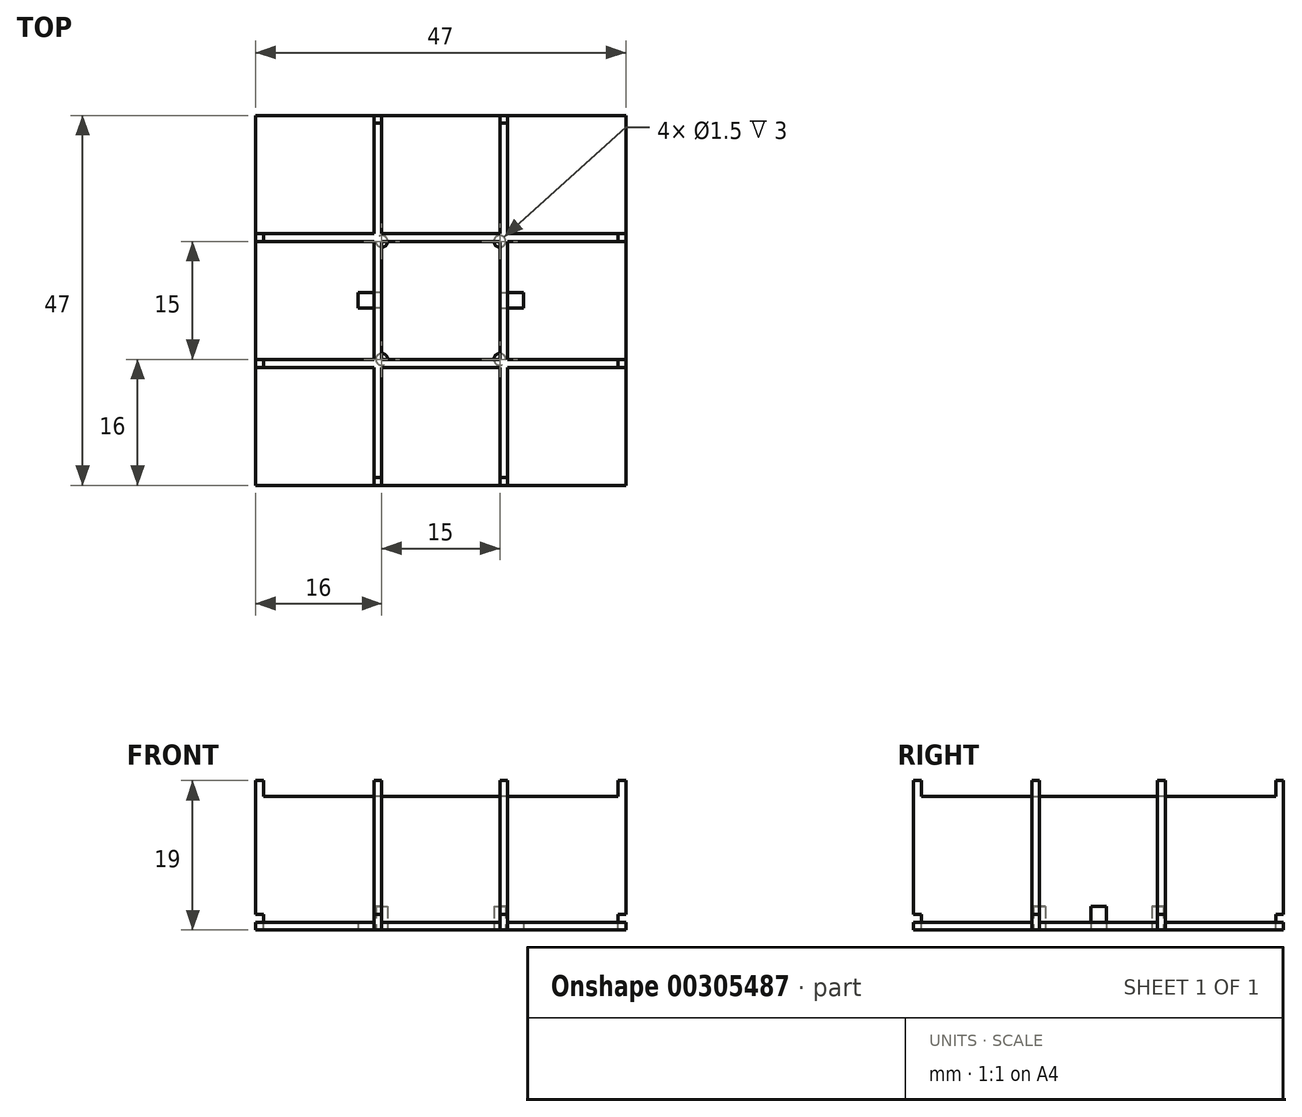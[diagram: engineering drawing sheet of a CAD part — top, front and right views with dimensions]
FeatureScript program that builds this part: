
annotation { "Feature Type Name" : "Feature", "Feature Type Description" : "" }
export const myFeature = defineFeature(function(context is Context, id is Id, definition is map)
    precondition{}
    {
        {
            var Q0;
            Q0=qCreatedBy(makeId("Top.planeOp"),FACE);
            var sketch = newSketch(context, id + "F0", { "sketchPlane" : qUnion([Q0])});
            skLineSegment(sketch, "E0.bottom", {"start": v(-23.5, 23.5) * mm, "end": v(23.5, 23.5) * mm});
            skLineSegment(sketch, "E0.top", {"start": v(-23.5, -23.5) * mm, "end": v(23.5, -23.5) * mm});
            skLineSegment(sketch, "E0.left", {"start": v(-23.5, 23.5) * mm, "end": v(-23.5, -23.5) * mm});
            skLineSegment(sketch, "E0.right", {"start": v(23.5, 23.5) * mm, "end": v(23.5, -23.5) * mm});
            skLineSegment(sketch, "E1", {"start": v(0, 26.11) * mm, "end": v(0, -40.09) * mm, "construction": true});
            skLineSegment(sketch, "E2", {"start": v(37.07, 0) * mm, "end": v(-38.69, 0) * mm, "construction": true});
            skLineSegment(sketch, "E3", {"start": v(-23.5, 8.5) * mm, "end": v(23.5, 8.5) * mm});
            skLineSegment(sketch, "E4", {"start": v(23.5, -8.5) * mm, "end": v(-23.5, -8.5) * mm});
            skLineSegment(sketch, "E5", {"start": v(-8.5, 23.5) * mm, "end": v(-8.5, -23.5) * mm});
            skLineSegment(sketch, "E6", {"start": v(8.5, 23.5) * mm, "end": v(8.5, -23.5) * mm});
            skLineSegment(sketch, "E7.0", {"start": v(-23.5, 7.5) * mm, "end": v(23.5, 7.5) * mm});
            skLineSegment(sketch, "E8.0", {"start": v(23.5, -7.5) * mm, "end": v(-23.5, -7.5) * mm});
            skLineSegment(sketch, "E9.0", {"start": v(-7.5, 23.5) * mm, "end": v(-7.5, -23.5) * mm});
            skLineSegment(sketch, "E10.0", {"start": v(7.5, 23.5) * mm, "end": v(7.5, -23.5) * mm});
            skSolve(sketch);
        }
        {
            var Q0;
            {var subQ0=sQuery(id+"F0.wireOp",EDGE,"E7.0");var subQ1=sQuery(id+"F0.wireOp",EDGE,"E6");var subQ2=makeQuery(id+"F0.imprint","INTERSECT",VERTEX,{"derivedFrom":[subQ1,subQ0]});Q0=makeQuery(id+"F0.imprint","IMPRINT",FACE,{"disambiguationData":[TD([[makeQuery(id+"F0.imprint","IMPRINT",EDGE,{"disambiguationData":[TD([[subQ2,-1.0]])],"derivedFrom":subQ1}),-1.0]])]});}
            var Q1;
            {var subQ0=sQuery(id+"F0.wireOp",EDGE,"E4");var subQ1=sQuery(id+"F0.wireOp",EDGE,"E0.left");var subQ2=makeQuery(id+"F0.imprint","INTERSECT",VERTEX,{"derivedFrom":[subQ1,subQ0]});Q1=makeQuery(id+"F0.imprint","IMPRINT",FACE,{"disambiguationData":[TD([[makeQuery(id+"F0.imprint","IMPRINT",EDGE,{"disambiguationData":[TD([[subQ2,1.0]])],"derivedFrom":subQ1}),1.0]])]});}
            var Q2;
            {var subQ0=sQuery(id+"F0.wireOp",EDGE,"E7.0");var subQ1=sQuery(id+"F0.wireOp",EDGE,"E0.left");var subQ2=makeQuery(id+"F0.imprint","INTERSECT",VERTEX,{"derivedFrom":[subQ1,subQ0]});Q2=makeQuery(id+"F0.imprint","IMPRINT",FACE,{"disambiguationData":[TD([[makeQuery(id+"F0.imprint","IMPRINT",EDGE,{"disambiguationData":[TD([[subQ2,-1.0]])],"derivedFrom":subQ1}),1.0]])]});}
            var Q3;
            {var subQ0=sQuery(id+"F0.wireOp",EDGE,"E6");var subQ1=sQuery(id+"F0.wireOp",EDGE,"E0.top");var subQ2=makeQuery(id+"F0.imprint","INTERSECT",VERTEX,{"derivedFrom":[subQ1,subQ0]});Q3=makeQuery(id+"F0.imprint","IMPRINT",FACE,{"disambiguationData":[TD([[makeQuery(id+"F0.imprint","IMPRINT",EDGE,{"disambiguationData":[TD([[subQ2,1.0]])],"derivedFrom":subQ1}),1.0]])]});}
            var Q4;
            {var subQ0=sQuery(id+"F0.wireOp",EDGE,"E9.0");var subQ1=sQuery(id+"F0.wireOp",EDGE,"E0.top");var subQ2=makeQuery(id+"F0.imprint","INTERSECT",VERTEX,{"derivedFrom":[subQ1,subQ0]});Q4=makeQuery(id+"F0.imprint","IMPRINT",FACE,{"disambiguationData":[TD([[makeQuery(id+"F0.imprint","IMPRINT",EDGE,{"disambiguationData":[TD([[subQ2,-1.0]])],"derivedFrom":subQ1}),1.0]])]});}
            var Q5;
            {var subQ0=sQuery(id+"F0.wireOp",EDGE,"E5");var subQ1=sQuery(id+"F0.wireOp",EDGE,"E0.top");var subQ2=makeQuery(id+"F0.imprint","INTERSECT",VERTEX,{"derivedFrom":[subQ1,subQ0]});Q5=makeQuery(id+"F0.imprint","IMPRINT",FACE,{"disambiguationData":[TD([[makeQuery(id+"F0.imprint","IMPRINT",EDGE,{"disambiguationData":[TD([[subQ2,-1.0]])],"derivedFrom":subQ1}),1.0]])]});}
            var Q6;
            {var subQ0=sQuery(id+"F0.wireOp",EDGE,"E0.right");var subQ1=sQuery(id+"F0.wireOp",EDGE,"E0.top");var subQ2=makeQuery(id+"F0.imprint","INTERSECT",VERTEX,{"derivedFrom":[subQ1,subQ0]});Q6=makeQuery(id+"F0.imprint","IMPRINT",FACE,{"disambiguationData":[TD([[makeQuery(id+"F0.imprint","IMPRINT",EDGE,{"disambiguationData":[TD([[subQ2,1.0]])],"derivedFrom":subQ1}),1.0]])]});}
            var Q7;
            {var subQ0=sQuery(id+"F0.wireOp",EDGE,"E0.left");var subQ1=sQuery(id+"F0.wireOp",EDGE,"E0.top");var subQ2=makeQuery(id+"F0.imprint","INTERSECT",VERTEX,{"derivedFrom":[subQ1,subQ0]});Q7=makeQuery(id+"F0.imprint","IMPRINT",FACE,{"disambiguationData":[TD([[makeQuery(id+"F0.imprint","IMPRINT",EDGE,{"disambiguationData":[TD([[subQ2,-1.0]])],"derivedFrom":subQ1}),1.0]])]});}
            var Q8;
            {var subQ0=sQuery(id+"F0.wireOp",EDGE,"E7.0");var subQ1=sQuery(id+"F0.wireOp",EDGE,"E0.right");var subQ2=makeQuery(id+"F0.imprint","INTERSECT",VERTEX,{"derivedFrom":[subQ1,subQ0]});Q8=makeQuery(id+"F0.imprint","IMPRINT",FACE,{"disambiguationData":[TD([[makeQuery(id+"F0.imprint","IMPRINT",EDGE,{"disambiguationData":[TD([[subQ2,-1.0]])],"derivedFrom":subQ1}),-1.0]])]});}
            var Q9;
            {var subQ0=sQuery(id+"F0.wireOp",EDGE,"E4");var subQ1=sQuery(id+"F0.wireOp",EDGE,"E0.right");var subQ2=makeQuery(id+"F0.imprint","INTERSECT",VERTEX,{"derivedFrom":[subQ1,subQ0]});Q9=makeQuery(id+"F0.imprint","IMPRINT",FACE,{"disambiguationData":[TD([[makeQuery(id+"F0.imprint","IMPRINT",EDGE,{"disambiguationData":[TD([[subQ2,1.0]])],"derivedFrom":subQ1}),-1.0]])]});}
            var Q10;
            {var subQ0=sQuery(id+"F0.wireOp",EDGE,"E10.0");var subQ1=sQuery(id+"F0.wireOp",EDGE,"E4");var subQ2=makeQuery(id+"F0.imprint","INTERSECT",VERTEX,{"derivedFrom":[subQ1,subQ0]});Q10=makeQuery(id+"F0.imprint","IMPRINT",FACE,{"disambiguationData":[TD([[makeQuery(id+"F0.imprint","IMPRINT",EDGE,{"disambiguationData":[TD([[subQ2,-1.0]])],"derivedFrom":subQ1}),-1.0]])]});}
            var Q11;
            {var subQ0=sQuery(id+"F0.wireOp",EDGE,"E7.0");var subQ1=sQuery(id+"F0.wireOp",EDGE,"E5");var subQ2=makeQuery(id+"F0.imprint","INTERSECT",VERTEX,{"derivedFrom":[subQ1,subQ0]});Q11=makeQuery(id+"F0.imprint","IMPRINT",FACE,{"disambiguationData":[TD([[makeQuery(id+"F0.imprint","IMPRINT",EDGE,{"disambiguationData":[TD([[subQ2,-1.0]])],"derivedFrom":subQ1}),1.0]])]});}
            var Q12;
            {var subQ0=sQuery(id+"F0.wireOp",EDGE,"E9.0");var subQ1=sQuery(id+"F0.wireOp",EDGE,"E7.0");var subQ2=makeQuery(id+"F0.imprint","INTERSECT",VERTEX,{"derivedFrom":[subQ1,subQ0]});Q12=makeQuery(id+"F0.imprint","IMPRINT",FACE,{"disambiguationData":[TD([[makeQuery(id+"F0.imprint","IMPRINT",EDGE,{"disambiguationData":[TD([[subQ2,-1.0]])],"derivedFrom":subQ1}),-1.0]])]});}
            var Q13;
            {var subQ0=sQuery(id+"F0.wireOp",EDGE,"E6");var subQ1=sQuery(id+"F0.wireOp",EDGE,"E4");var subQ2=makeQuery(id+"F0.imprint","INTERSECT",VERTEX,{"derivedFrom":[subQ1,subQ0]});Q13=makeQuery(id+"F0.imprint","IMPRINT",FACE,{"disambiguationData":[TD([[makeQuery(id+"F0.imprint","IMPRINT",EDGE,{"disambiguationData":[TD([[subQ2,-1.0]])],"derivedFrom":subQ1}),-1.0]])]});}
            var Q14;
            {var subQ0=sQuery(id+"F0.wireOp",EDGE,"E9.0");var subQ1=sQuery(id+"F0.wireOp",EDGE,"E4");var subQ2=makeQuery(id+"F0.imprint","INTERSECT",VERTEX,{"derivedFrom":[subQ1,subQ0]});Q14=makeQuery(id+"F0.imprint","IMPRINT",FACE,{"disambiguationData":[TD([[makeQuery(id+"F0.imprint","IMPRINT",EDGE,{"disambiguationData":[TD([[subQ2,-1.0]])],"derivedFrom":subQ1}),-1.0]])]});}
            var Q15;
            {var subQ0=sQuery(id+"F0.wireOp",EDGE,"E5");var subQ1=sQuery(id+"F0.wireOp",EDGE,"E3");var subQ2=makeQuery(id+"F0.imprint","INTERSECT",VERTEX,{"derivedFrom":[subQ1,subQ0]});Q15=makeQuery(id+"F0.imprint","IMPRINT",FACE,{"disambiguationData":[TD([[makeQuery(id+"F0.imprint","IMPRINT",EDGE,{"disambiguationData":[TD([[subQ2,-1.0]])],"derivedFrom":subQ1}),-1.0]])]});}
            var Q16;
            {var subQ0=sQuery(id+"F0.wireOp",EDGE,"E3");var subQ1=sQuery(id+"F0.wireOp",EDGE,"E0.left");var subQ2=makeQuery(id+"F0.imprint","INTERSECT",VERTEX,{"derivedFrom":[subQ1,subQ0]});Q16=makeQuery(id+"F0.imprint","IMPRINT",FACE,{"disambiguationData":[TD([[makeQuery(id+"F0.imprint","IMPRINT",EDGE,{"disambiguationData":[TD([[subQ2,-1.0]])],"derivedFrom":subQ1}),1.0]])]});}
            var Q17;
            {var subQ0=sQuery(id+"F0.wireOp",EDGE,"E6");var subQ1=sQuery(id+"F0.wireOp",EDGE,"E0.bottom");var subQ2=makeQuery(id+"F0.imprint","INTERSECT",VERTEX,{"derivedFrom":[subQ1,subQ0]});Q17=makeQuery(id+"F0.imprint","IMPRINT",FACE,{"disambiguationData":[TD([[makeQuery(id+"F0.imprint","IMPRINT",EDGE,{"disambiguationData":[TD([[subQ2,1.0]])],"derivedFrom":subQ1}),-1.0]])]});}
            var Q18;
            {var subQ0=sQuery(id+"F0.wireOp",EDGE,"E9.0");var subQ1=sQuery(id+"F0.wireOp",EDGE,"E0.bottom");var subQ2=makeQuery(id+"F0.imprint","INTERSECT",VERTEX,{"derivedFrom":[subQ1,subQ0]});Q18=makeQuery(id+"F0.imprint","IMPRINT",FACE,{"disambiguationData":[TD([[makeQuery(id+"F0.imprint","IMPRINT",EDGE,{"disambiguationData":[TD([[subQ2,-1.0]])],"derivedFrom":subQ1}),-1.0]])]});}
            var Q19;
            {var subQ0=sQuery(id+"F0.wireOp",EDGE,"E5");var subQ1=sQuery(id+"F0.wireOp",EDGE,"E0.bottom");var subQ2=makeQuery(id+"F0.imprint","INTERSECT",VERTEX,{"derivedFrom":[subQ1,subQ0]});Q19=makeQuery(id+"F0.imprint","IMPRINT",FACE,{"disambiguationData":[TD([[makeQuery(id+"F0.imprint","IMPRINT",EDGE,{"disambiguationData":[TD([[subQ2,-1.0]])],"derivedFrom":subQ1}),-1.0]])]});}
            var Q20;
            {var subQ0=sQuery(id+"F0.wireOp",EDGE,"E0.right");var subQ1=sQuery(id+"F0.wireOp",EDGE,"E0.bottom");var subQ2=makeQuery(id+"F0.imprint","INTERSECT",VERTEX,{"derivedFrom":[subQ1,subQ0]});Q20=makeQuery(id+"F0.imprint","IMPRINT",FACE,{"disambiguationData":[TD([[makeQuery(id+"F0.imprint","IMPRINT",EDGE,{"disambiguationData":[TD([[subQ2,1.0]])],"derivedFrom":subQ1}),-1.0]])]});}
            var Q21;
            {var subQ0=sQuery(id+"F0.wireOp",EDGE,"E3");var subQ1=sQuery(id+"F0.wireOp",EDGE,"E0.right");var subQ2=makeQuery(id+"F0.imprint","INTERSECT",VERTEX,{"derivedFrom":[subQ1,subQ0]});Q21=makeQuery(id+"F0.imprint","IMPRINT",FACE,{"disambiguationData":[TD([[makeQuery(id+"F0.imprint","IMPRINT",EDGE,{"disambiguationData":[TD([[subQ2,-1.0]])],"derivedFrom":subQ1}),-1.0]])]});}
            var Q22;
            {var subQ0=sQuery(id+"F0.wireOp",EDGE,"E0.left");var subQ1=sQuery(id+"F0.wireOp",EDGE,"E0.bottom");var subQ2=makeQuery(id+"F0.imprint","INTERSECT",VERTEX,{"derivedFrom":[subQ1,subQ0]});Q22=makeQuery(id+"F0.imprint","IMPRINT",FACE,{"disambiguationData":[TD([[makeQuery(id+"F0.imprint","IMPRINT",EDGE,{"disambiguationData":[TD([[subQ2,-1.0]])],"derivedFrom":subQ1}),-1.0]])]});}
            var Q23;
            {var subQ0=sQuery(id+"F0.wireOp",EDGE,"E10.0");var subQ1=sQuery(id+"F0.wireOp",EDGE,"E3");var subQ2=makeQuery(id+"F0.imprint","INTERSECT",VERTEX,{"derivedFrom":[subQ1,subQ0]});Q23=makeQuery(id+"F0.imprint","IMPRINT",FACE,{"disambiguationData":[TD([[makeQuery(id+"F0.imprint","IMPRINT",EDGE,{"disambiguationData":[TD([[subQ2,-1.0]])],"derivedFrom":subQ1}),-1.0]])]});}
            var Q24;
            {var subQ0=sQuery(id+"F0.wireOp",EDGE,"E9.0");var subQ1=sQuery(id+"F0.wireOp",EDGE,"E3");var subQ2=makeQuery(id+"F0.imprint","INTERSECT",VERTEX,{"derivedFrom":[subQ1,subQ0]});Q24=makeQuery(id+"F0.imprint","IMPRINT",FACE,{"disambiguationData":[TD([[makeQuery(id+"F0.imprint","IMPRINT",EDGE,{"disambiguationData":[TD([[subQ2,-1.0]])],"derivedFrom":subQ1}),-1.0]])]});}
            extrude(context, id + "F1", {"entities" : qUnion([Q0, Q1, Q2, Q3, Q4, Q5, Q6, Q7, Q8, Q9, Q10, Q11, Q12, Q13, Q14, Q15, Q16, Q17, Q18, Q19, Q20, Q21, Q22, Q23, Q24]), "oppositeDirection" : true, "depth" : 1 * mm});
        }
        {
            var Q0;
            {var subQ0=sQuery(id+"F0.wireOp",EDGE,"E9.0");var subQ1=sQuery(id+"F0.wireOp",EDGE,"E4");var subQ2=makeQuery(id+"F0.imprint","INTERSECT",VERTEX,{"derivedFrom":[subQ1,subQ0]});Q0=makeQuery(id+"F0.imprint","IMPRINT",FACE,{"disambiguationData":[TD([[makeQuery(id+"F0.imprint","IMPRINT",EDGE,{"disambiguationData":[TD([[subQ2,-1.0]])],"derivedFrom":subQ1}),-1.0]])]});}
            var Q1;
            {var subQ0=sQuery(id+"F0.wireOp",EDGE,"E6");var subQ1=sQuery(id+"F0.wireOp",EDGE,"E4");var subQ2=makeQuery(id+"F0.imprint","INTERSECT",VERTEX,{"derivedFrom":[subQ1,subQ0]});Q1=makeQuery(id+"F0.imprint","IMPRINT",FACE,{"disambiguationData":[TD([[makeQuery(id+"F0.imprint","IMPRINT",EDGE,{"disambiguationData":[TD([[subQ2,-1.0]])],"derivedFrom":subQ1}),-1.0]])]});}
            var Q2;
            {var subQ0=sQuery(id+"F0.wireOp",EDGE,"E5");var subQ1=sQuery(id+"F0.wireOp",EDGE,"E3");var subQ2=makeQuery(id+"F0.imprint","INTERSECT",VERTEX,{"derivedFrom":[subQ1,subQ0]});Q2=makeQuery(id+"F0.imprint","IMPRINT",FACE,{"disambiguationData":[TD([[makeQuery(id+"F0.imprint","IMPRINT",EDGE,{"disambiguationData":[TD([[subQ2,-1.0]])],"derivedFrom":subQ1}),-1.0]])]});}
            var Q3;
            {var subQ0=sQuery(id+"F0.wireOp",EDGE,"E10.0");var subQ1=sQuery(id+"F0.wireOp",EDGE,"E3");var subQ2=makeQuery(id+"F0.imprint","INTERSECT",VERTEX,{"derivedFrom":[subQ1,subQ0]});Q3=makeQuery(id+"F0.imprint","IMPRINT",FACE,{"disambiguationData":[TD([[makeQuery(id+"F0.imprint","IMPRINT",EDGE,{"disambiguationData":[TD([[subQ2,-1.0]])],"derivedFrom":subQ1}),-1.0]])]});}
            var Q4;
            {var subQ0=sQuery(id+"F0.wireOp",EDGE,"E3");var subQ1=sQuery(id+"F0.wireOp",EDGE,"E0.right");var subQ2=makeQuery(id+"F0.imprint","INTERSECT",VERTEX,{"derivedFrom":[subQ1,subQ0]});Q4=makeQuery(id+"F0.imprint","IMPRINT",FACE,{"disambiguationData":[TD([[makeQuery(id+"F0.imprint","IMPRINT",EDGE,{"disambiguationData":[TD([[subQ2,-1.0]])],"derivedFrom":subQ1}),-1.0]])]});}
            var Q5;
            {var subQ0=sQuery(id+"F0.wireOp",EDGE,"E6");var subQ1=sQuery(id+"F0.wireOp",EDGE,"E0.bottom");var subQ2=makeQuery(id+"F0.imprint","INTERSECT",VERTEX,{"derivedFrom":[subQ1,subQ0]});Q5=makeQuery(id+"F0.imprint","IMPRINT",FACE,{"disambiguationData":[TD([[makeQuery(id+"F0.imprint","IMPRINT",EDGE,{"disambiguationData":[TD([[subQ2,1.0]])],"derivedFrom":subQ1}),-1.0]])]});}
            var Q6;
            {var subQ0=sQuery(id+"F0.wireOp",EDGE,"E5");var subQ1=sQuery(id+"F0.wireOp",EDGE,"E0.bottom");var subQ2=makeQuery(id+"F0.imprint","INTERSECT",VERTEX,{"derivedFrom":[subQ1,subQ0]});Q6=makeQuery(id+"F0.imprint","IMPRINT",FACE,{"disambiguationData":[TD([[makeQuery(id+"F0.imprint","IMPRINT",EDGE,{"disambiguationData":[TD([[subQ2,-1.0]])],"derivedFrom":subQ1}),-1.0]])]});}
            var Q7;
            {var subQ0=sQuery(id+"F0.wireOp",EDGE,"E9.0");var subQ1=sQuery(id+"F0.wireOp",EDGE,"E3");var subQ2=makeQuery(id+"F0.imprint","INTERSECT",VERTEX,{"derivedFrom":[subQ1,subQ0]});Q7=makeQuery(id+"F0.imprint","IMPRINT",FACE,{"disambiguationData":[TD([[makeQuery(id+"F0.imprint","IMPRINT",EDGE,{"disambiguationData":[TD([[subQ2,-1.0]])],"derivedFrom":subQ1}),-1.0]])]});}
            var Q8;
            {var subQ0=sQuery(id+"F0.wireOp",EDGE,"E3");var subQ1=sQuery(id+"F0.wireOp",EDGE,"E0.left");var subQ2=makeQuery(id+"F0.imprint","INTERSECT",VERTEX,{"derivedFrom":[subQ1,subQ0]});Q8=makeQuery(id+"F0.imprint","IMPRINT",FACE,{"disambiguationData":[TD([[makeQuery(id+"F0.imprint","IMPRINT",EDGE,{"disambiguationData":[TD([[subQ2,-1.0]])],"derivedFrom":subQ1}),1.0]])]});}
            var Q9;
            {var subQ0=sQuery(id+"F0.wireOp",EDGE,"E7.0");var subQ1=sQuery(id+"F0.wireOp",EDGE,"E5");var subQ2=makeQuery(id+"F0.imprint","INTERSECT",VERTEX,{"derivedFrom":[subQ1,subQ0]});Q9=makeQuery(id+"F0.imprint","IMPRINT",FACE,{"disambiguationData":[TD([[makeQuery(id+"F0.imprint","IMPRINT",EDGE,{"disambiguationData":[TD([[subQ2,-1.0]])],"derivedFrom":subQ1}),1.0]])]});}
            var Q10;
            {var subQ0=sQuery(id+"F0.wireOp",EDGE,"E4");var subQ1=sQuery(id+"F0.wireOp",EDGE,"E0.left");var subQ2=makeQuery(id+"F0.imprint","INTERSECT",VERTEX,{"derivedFrom":[subQ1,subQ0]});Q10=makeQuery(id+"F0.imprint","IMPRINT",FACE,{"disambiguationData":[TD([[makeQuery(id+"F0.imprint","IMPRINT",EDGE,{"disambiguationData":[TD([[subQ2,1.0]])],"derivedFrom":subQ1}),1.0]])]});}
            var Q11;
            {var subQ0=sQuery(id+"F0.wireOp",EDGE,"E10.0");var subQ1=sQuery(id+"F0.wireOp",EDGE,"E4");var subQ2=makeQuery(id+"F0.imprint","INTERSECT",VERTEX,{"derivedFrom":[subQ1,subQ0]});Q11=makeQuery(id+"F0.imprint","IMPRINT",FACE,{"disambiguationData":[TD([[makeQuery(id+"F0.imprint","IMPRINT",EDGE,{"disambiguationData":[TD([[subQ2,-1.0]])],"derivedFrom":subQ1}),-1.0]])]});}
            var Q12;
            {var subQ0=sQuery(id+"F0.wireOp",EDGE,"E4");var subQ1=sQuery(id+"F0.wireOp",EDGE,"E0.right");var subQ2=makeQuery(id+"F0.imprint","INTERSECT",VERTEX,{"derivedFrom":[subQ1,subQ0]});Q12=makeQuery(id+"F0.imprint","IMPRINT",FACE,{"disambiguationData":[TD([[makeQuery(id+"F0.imprint","IMPRINT",EDGE,{"disambiguationData":[TD([[subQ2,1.0]])],"derivedFrom":subQ1}),-1.0]])]});}
            var Q13;
            {var subQ0=sQuery(id+"F0.wireOp",EDGE,"E6");var subQ1=sQuery(id+"F0.wireOp",EDGE,"E0.top");var subQ2=makeQuery(id+"F0.imprint","INTERSECT",VERTEX,{"derivedFrom":[subQ1,subQ0]});Q13=makeQuery(id+"F0.imprint","IMPRINT",FACE,{"disambiguationData":[TD([[makeQuery(id+"F0.imprint","IMPRINT",EDGE,{"disambiguationData":[TD([[subQ2,1.0]])],"derivedFrom":subQ1}),1.0]])]});}
            var Q14;
            {var subQ0=sQuery(id+"F0.wireOp",EDGE,"E5");var subQ1=sQuery(id+"F0.wireOp",EDGE,"E0.top");var subQ2=makeQuery(id+"F0.imprint","INTERSECT",VERTEX,{"derivedFrom":[subQ1,subQ0]});Q14=makeQuery(id+"F0.imprint","IMPRINT",FACE,{"disambiguationData":[TD([[makeQuery(id+"F0.imprint","IMPRINT",EDGE,{"disambiguationData":[TD([[subQ2,-1.0]])],"derivedFrom":subQ1}),1.0]])]});}
            var Q15;
            {var subQ0=sQuery(id+"F0.wireOp",EDGE,"E7.0");var subQ1=sQuery(id+"F0.wireOp",EDGE,"E6");var subQ2=makeQuery(id+"F0.imprint","INTERSECT",VERTEX,{"derivedFrom":[subQ1,subQ0]});Q15=makeQuery(id+"F0.imprint","IMPRINT",FACE,{"disambiguationData":[TD([[makeQuery(id+"F0.imprint","IMPRINT",EDGE,{"disambiguationData":[TD([[subQ2,-1.0]])],"derivedFrom":subQ1}),-1.0]])]});}
            extrude(context, id + "F2", {"entities" : qUnion([Q0, Q1, Q2, Q3, Q4, Q5, Q6, Q7, Q8, Q9, Q10, Q11, Q12, Q13, Q14, Q15]), "operationType" : NewBodyOperationType.ADD, "depth" : 16 * mm});
        }
        {
            var Q0;
            Q0=makeQuery(id+"F1.opExtrude","CAP_FACE",FACE,{"disambiguationData":[OSD([sQuery(id+"F0.wireOp",EDGE,"E0.bottom"),sQuery(id+"F0.wireOp",EDGE,"E0.top"),sQuery(id+"F0.wireOp",EDGE,"E0.left"),sQuery(id+"F0.wireOp",EDGE,"E0.right")])],"isStart":false});
            var sketch = newSketch(context, id + "F3", { "sketchPlane" : qUnion([Q0])});
            skLineSegment(sketch, "E11.bottom", {"start": v(-7.5, 7.5) * mm, "end": v(7.5, 7.5) * mm});
            skLineSegment(sketch, "E11.top", {"start": v(-7.5, -7.5) * mm, "end": v(7.5, -7.5) * mm});
            skLineSegment(sketch, "E11.left", {"start": v(-7.5, 7.5) * mm, "end": v(-7.5, -7.5) * mm});
            skLineSegment(sketch, "E11.right", {"start": v(7.5, 7.5) * mm, "end": v(7.5, -7.5) * mm});
            skLineSegment(sketch, "E12.0", {"start": v(7.5, 8.5) * mm, "end": v(-7.5, 8.5) * mm, "construction": true});
            skLineSegment(sketch, "E13", {"start": v(0, 19.4) * mm, "end": v(0, -17.52) * mm, "construction": true});
            skLineSegment(sketch, "E14", {"start": v(14.3, 0) * mm, "end": v(-21.62, 0) * mm, "construction": true});
            skPoint(sketch, "E14.endSnap0", {"position": v(-23.5, 0) * mm});
            skLineSegment(sketch, "E15.0", {"start": v(10.5, 10.5) * mm, "end": v(10.5, -10.5) * mm});
            skLineSegment(sketch, "E15.1", {"start": v(-10.5, 10.5) * mm, "end": v(10.5, 10.5) * mm});
            skLineSegment(sketch, "E15.2", {"start": v(-10.5, 10.5) * mm, "end": v(-10.5, -10.5) * mm});
            skLineSegment(sketch, "E15.3", {"start": v(-10.5, -10.5) * mm, "end": v(10.5, -10.5) * mm});
            skLineSegment(sketch, "E16.bottom", {"start": v(-7.5, 1) * mm, "end": v(-10.5, 1) * mm});
            skLineSegment(sketch, "E16.top", {"start": v(-7.5, -1) * mm, "end": v(-10.5, -1) * mm});
            skLineSegment(sketch, "E16.left", {"start": v(-7.5, 1) * mm, "end": v(-7.5, -1) * mm});
            skLineSegment(sketch, "E16.right", {"start": v(-10.5, 1) * mm, "end": v(-10.5, -1) * mm});
            skLineSegment(sketch, "E17.bottom", {"start": v(-1, 10.5) * mm, "end": v(1, 10.5) * mm});
            skLineSegment(sketch, "E17.top", {"start": v(-1, 7.5) * mm, "end": v(1, 7.5) * mm});
            skLineSegment(sketch, "E17.left", {"start": v(-1, 10.5) * mm, "end": v(-1, 7.5) * mm});
            skLineSegment(sketch, "E17.right", {"start": v(1, 10.5) * mm, "end": v(1, 7.5) * mm});
            skLineSegment(sketch, "E18.bottom", {"start": v(7.5, 1) * mm, "end": v(10.5, 1) * mm});
            skLineSegment(sketch, "E18.top", {"start": v(7.5, -1) * mm, "end": v(10.5, -1) * mm});
            skLineSegment(sketch, "E18.left", {"start": v(7.5, 1) * mm, "end": v(7.5, -1) * mm});
            skLineSegment(sketch, "E18.right", {"start": v(10.5, 1) * mm, "end": v(10.5, -1) * mm});
            skLineSegment(sketch, "E19.bottom", {"start": v(1, -7.5) * mm, "end": v(-1, -7.5) * mm});
            skLineSegment(sketch, "E19.top", {"start": v(1, -10.5) * mm, "end": v(-1, -10.5) * mm});
            skLineSegment(sketch, "E19.left", {"start": v(1, -7.5) * mm, "end": v(1, -10.5) * mm});
            skLineSegment(sketch, "E19.right", {"start": v(-1, -7.5) * mm, "end": v(-1, -10.5) * mm});
            skLineSegment(sketch, "E20.bottom", {"start": v(-10.5, 10.5) * mm, "end": v(-7.5, 10.5) * mm});
            skLineSegment(sketch, "E20.top", {"start": v(-10.5, 7.5) * mm, "end": v(-7.5, 7.5) * mm});
            skLineSegment(sketch, "E20.left", {"start": v(-10.5, 10.5) * mm, "end": v(-10.5, 7.5) * mm});
            skLineSegment(sketch, "E20.right", {"start": v(-7.5, 10.5) * mm, "end": v(-7.5, 7.5) * mm});
            skLineSegment(sketch, "E21.bottom", {"start": v(10.5, 10.5) * mm, "end": v(7.5, 10.5) * mm});
            skLineSegment(sketch, "E21.top", {"start": v(10.5, 7.5) * mm, "end": v(7.5, 7.5) * mm});
            skLineSegment(sketch, "E21.left", {"start": v(10.5, 10.5) * mm, "end": v(10.5, 7.5) * mm});
            skLineSegment(sketch, "E21.right", {"start": v(7.5, 10.5) * mm, "end": v(7.5, 7.5) * mm});
            skLineSegment(sketch, "E22.bottom", {"start": v(10.5, -10.5) * mm, "end": v(7.5, -10.5) * mm});
            skLineSegment(sketch, "E22.top", {"start": v(10.5, -7.5) * mm, "end": v(7.5, -7.5) * mm});
            skLineSegment(sketch, "E22.left", {"start": v(10.5, -10.5) * mm, "end": v(10.5, -7.5) * mm});
            skLineSegment(sketch, "E22.right", {"start": v(7.5, -10.5) * mm, "end": v(7.5, -7.5) * mm});
            skLineSegment(sketch, "E23.bottom", {"start": v(-10.5, -10.5) * mm, "end": v(-7.5, -10.5) * mm});
            skLineSegment(sketch, "E23.top", {"start": v(-10.5, -7.5) * mm, "end": v(-7.5, -7.5) * mm});
            skLineSegment(sketch, "E23.left", {"start": v(-10.5, -10.5) * mm, "end": v(-10.5, -7.5) * mm});
            skLineSegment(sketch, "E23.right", {"start": v(-7.5, -10.5) * mm, "end": v(-7.5, -7.5) * mm});
            skCircle(sketch, "E24", {"center": v(-7.5, -7.5) * mm, "radius": 0.75 * mm});
            skCircle(sketch, "E25", {"center": v(7.5, -7.5) * mm, "radius": 0.75 * mm});
            skCircle(sketch, "E26", {"center": v(7.5, 7.5) * mm, "radius": 0.75 * mm});
            skCircle(sketch, "E27", {"center": v(-7.5, 7.5) * mm, "radius": 0.75 * mm});
            skSolve(sketch);
        }
        {
            var Q0;
            Q0=makeQuery(id+"F3.imprint","IMPRINT",FACE,{"disambiguationData":[TD([[makeQuery(id+"F3.imprint","IMPRINT",EDGE,{"derivedFrom":sQuery(id+"F3.wireOp",EDGE,"E17.bottom")}),-1.0]])]});
            var Q1;
            Q1=makeQuery(id+"F3.imprint","IMPRINT",FACE,{"disambiguationData":[TD([[makeQuery(id+"F3.imprint","IMPRINT",EDGE,{"derivedFrom":sQuery(id+"F3.wireOp",EDGE,"E18.bottom")}),-1.0]])]});
            var Q2;
            Q2=makeQuery(id+"F3.imprint","IMPRINT",FACE,{"disambiguationData":[TD([[makeQuery(id+"F3.imprint","IMPRINT",EDGE,{"derivedFrom":sQuery(id+"F3.wireOp",EDGE,"E19.bottom")}),1.0]])]});
            var Q3;
            Q3=makeQuery(id+"F3.imprint","IMPRINT",FACE,{"disambiguationData":[TD([[makeQuery(id+"F3.imprint","IMPRINT",EDGE,{"derivedFrom":sQuery(id+"F3.wireOp",EDGE,"E16.bottom")}),1.0]])]});
            var Q4;
            {var subQ1=sQuery(id+"F3.wireOp",EDGE,"E16.left");Q4=makeQuery(id+"F3.imprint","IMPRINT",FACE,{"disambiguationData":[TD([[makeQuery(id+"F3.imprint","IMPRINT",EDGE,{"derivedFrom":subQ1}),1.0]])]});}
            var Q5;
            {var subQ1=sQuery(id+"F3.wireOp",EDGE,"E23.bottom");Q5=makeQuery(id+"F3.imprint","IMPRINT",FACE,{"disambiguationData":[TD([[makeQuery(id+"F3.imprint","IMPRINT",EDGE,{"derivedFrom":subQ1}),1.0]])]});}
            var Q6;
            {var subQ1=sQuery(id+"F3.wireOp",EDGE,"E22.bottom");Q6=makeQuery(id+"F3.imprint","IMPRINT",FACE,{"disambiguationData":[TD([[makeQuery(id+"F3.imprint","IMPRINT",EDGE,{"derivedFrom":subQ1}),-1.0]])]});}
            var Q7;
            {var subQ1=sQuery(id+"F3.wireOp",EDGE,"E21.bottom");Q7=makeQuery(id+"F3.imprint","IMPRINT",FACE,{"disambiguationData":[TD([[makeQuery(id+"F3.imprint","IMPRINT",EDGE,{"derivedFrom":subQ1}),1.0]])]});}
            var Q8;
            {var subQ1=sQuery(id+"F3.wireOp",EDGE,"E20.bottom");Q8=makeQuery(id+"F3.imprint","IMPRINT",FACE,{"disambiguationData":[TD([[makeQuery(id+"F3.imprint","IMPRINT",EDGE,{"derivedFrom":subQ1}),-1.0]])]});}
            var Q9;
            {var subQ1=sQuery(id+"F3.wireOp",EDGE,"E11.bottom");var subQ3=sQuery(id+"F3.wireOp",EDGE,"E27");var subQ4=makeQuery(id+"F3.imprint","INTERSECT",VERTEX,{"derivedFrom":[subQ1,subQ3]});Q9=makeQuery(id+"F3.imprint","IMPRINT",FACE,{"disambiguationData":[TD([[makeQuery(id+"F3.imprint","IMPRINT",EDGE,{"disambiguationData":[TD([[subQ4,-1.0]])],"derivedFrom":subQ3}),1.0]])]});}
            var Q10;
            {var subQ1=sQuery(id+"F3.wireOp",EDGE,"E11.left");var subQ3=sQuery(id+"F3.wireOp",EDGE,"E27");var subQ4=makeQuery(id+"F3.imprint","INTERSECT",VERTEX,{"derivedFrom":[subQ1,subQ3]});Q10=makeQuery(id+"F3.imprint","IMPRINT",FACE,{"disambiguationData":[TD([[makeQuery(id+"F3.imprint","IMPRINT",EDGE,{"disambiguationData":[TD([[subQ4,1.0]])],"derivedFrom":subQ3}),1.0]])]});}
            var Q11;
            {var subQ1=sQuery(id+"F3.wireOp",EDGE,"E11.bottom");var subQ3=sQuery(id+"F3.wireOp",EDGE,"E26");var subQ4=makeQuery(id+"F3.imprint","INTERSECT",VERTEX,{"derivedFrom":[subQ1,subQ3]});Q11=makeQuery(id+"F3.imprint","IMPRINT",FACE,{"disambiguationData":[TD([[makeQuery(id+"F3.imprint","IMPRINT",EDGE,{"disambiguationData":[TD([[subQ4,-1.0]])],"derivedFrom":subQ3}),1.0]])]});}
            var Q12;
            {var subQ1=sQuery(id+"F3.wireOp",EDGE,"E21.top");var subQ3=sQuery(id+"F3.wireOp",EDGE,"E26");var subQ4=makeQuery(id+"F3.imprint","INTERSECT",VERTEX,{"derivedFrom":[subQ1,subQ3]});Q12=makeQuery(id+"F3.imprint","IMPRINT",FACE,{"disambiguationData":[TD([[makeQuery(id+"F3.imprint","IMPRINT",EDGE,{"disambiguationData":[TD([[subQ4,-1.0]])],"derivedFrom":subQ3}),1.0]])]});}
            var Q13;
            {var subQ1=sQuery(id+"F3.wireOp",EDGE,"E11.bottom");var subQ3=sQuery(id+"F3.wireOp",EDGE,"E26");var subQ4=makeQuery(id+"F3.imprint","INTERSECT",VERTEX,{"derivedFrom":[subQ1,subQ3]});Q13=makeQuery(id+"F3.imprint","IMPRINT",FACE,{"disambiguationData":[TD([[makeQuery(id+"F3.imprint","IMPRINT",EDGE,{"disambiguationData":[TD([[subQ4,1.0]])],"derivedFrom":subQ3}),1.0]])]});}
            var Q14;
            {var subQ1=sQuery(id+"F3.wireOp",EDGE,"E11.right");var subQ3=sQuery(id+"F3.wireOp",EDGE,"E26");var subQ4=makeQuery(id+"F3.imprint","INTERSECT",VERTEX,{"derivedFrom":[subQ1,subQ3]});Q14=makeQuery(id+"F3.imprint","IMPRINT",FACE,{"disambiguationData":[TD([[makeQuery(id+"F3.imprint","IMPRINT",EDGE,{"disambiguationData":[TD([[subQ4,-1.0]])],"derivedFrom":subQ3}),1.0]])]});}
            var Q15;
            {var subQ1=sQuery(id+"F3.wireOp",EDGE,"E11.top");var subQ3=sQuery(id+"F3.wireOp",EDGE,"E25");var subQ4=makeQuery(id+"F3.imprint","INTERSECT",VERTEX,{"derivedFrom":[subQ1,subQ3]});Q15=makeQuery(id+"F3.imprint","IMPRINT",FACE,{"disambiguationData":[TD([[makeQuery(id+"F3.imprint","IMPRINT",EDGE,{"disambiguationData":[TD([[subQ4,1.0]])],"derivedFrom":subQ3}),1.0]])]});}
            var Q16;
            {var subQ1=sQuery(id+"F3.wireOp",EDGE,"E22.top");var subQ3=sQuery(id+"F3.wireOp",EDGE,"E25");var subQ4=makeQuery(id+"F3.imprint","INTERSECT",VERTEX,{"derivedFrom":[subQ1,subQ3]});Q16=makeQuery(id+"F3.imprint","IMPRINT",FACE,{"disambiguationData":[TD([[makeQuery(id+"F3.imprint","IMPRINT",EDGE,{"disambiguationData":[TD([[subQ4,1.0]])],"derivedFrom":subQ3}),1.0]])]});}
            var Q17;
            {var subQ1=sQuery(id+"F3.wireOp",EDGE,"E11.right");var subQ3=sQuery(id+"F3.wireOp",EDGE,"E25");var subQ4=makeQuery(id+"F3.imprint","INTERSECT",VERTEX,{"derivedFrom":[subQ1,subQ3]});Q17=makeQuery(id+"F3.imprint","IMPRINT",FACE,{"disambiguationData":[TD([[makeQuery(id+"F3.imprint","IMPRINT",EDGE,{"disambiguationData":[TD([[subQ4,1.0]])],"derivedFrom":subQ3}),1.0]])]});}
            var Q18;
            {var subQ1=sQuery(id+"F3.wireOp",EDGE,"E11.top");var subQ3=sQuery(id+"F3.wireOp",EDGE,"E25");var subQ4=makeQuery(id+"F3.imprint","INTERSECT",VERTEX,{"derivedFrom":[subQ1,subQ3]});Q18=makeQuery(id+"F3.imprint","IMPRINT",FACE,{"disambiguationData":[TD([[makeQuery(id+"F3.imprint","IMPRINT",EDGE,{"disambiguationData":[TD([[subQ4,-1.0]])],"derivedFrom":subQ3}),1.0]])]});}
            var Q19;
            {var subQ1=sQuery(id+"F3.wireOp",EDGE,"E23.top");var subQ3=sQuery(id+"F3.wireOp",EDGE,"E24");var subQ4=makeQuery(id+"F3.imprint","INTERSECT",VERTEX,{"derivedFrom":[subQ1,subQ3]});Q19=makeQuery(id+"F3.imprint","IMPRINT",FACE,{"disambiguationData":[TD([[makeQuery(id+"F3.imprint","IMPRINT",EDGE,{"disambiguationData":[TD([[subQ4,-1.0]])],"derivedFrom":subQ3}),1.0]])]});}
            var Q20;
            {var subQ1=sQuery(id+"F3.wireOp",EDGE,"E11.top");var subQ3=sQuery(id+"F3.wireOp",EDGE,"E24");var subQ4=makeQuery(id+"F3.imprint","INTERSECT",VERTEX,{"derivedFrom":[subQ1,subQ3]});Q20=makeQuery(id+"F3.imprint","IMPRINT",FACE,{"disambiguationData":[TD([[makeQuery(id+"F3.imprint","IMPRINT",EDGE,{"disambiguationData":[TD([[subQ4,-1.0]])],"derivedFrom":subQ3}),1.0]])]});}
            var Q21;
            {var subQ1=sQuery(id+"F3.wireOp",EDGE,"E11.left");var subQ3=sQuery(id+"F3.wireOp",EDGE,"E24");var subQ4=makeQuery(id+"F3.imprint","INTERSECT",VERTEX,{"derivedFrom":[subQ1,subQ3]});Q21=makeQuery(id+"F3.imprint","IMPRINT",FACE,{"disambiguationData":[TD([[makeQuery(id+"F3.imprint","IMPRINT",EDGE,{"disambiguationData":[TD([[subQ4,-1.0]])],"derivedFrom":subQ3}),1.0]])]});}
            var Q22;
            {var subQ1=sQuery(id+"F3.wireOp",EDGE,"E11.top");var subQ3=sQuery(id+"F3.wireOp",EDGE,"E24");var subQ4=makeQuery(id+"F3.imprint","INTERSECT",VERTEX,{"derivedFrom":[subQ1,subQ3]});Q22=makeQuery(id+"F3.imprint","IMPRINT",FACE,{"disambiguationData":[TD([[makeQuery(id+"F3.imprint","IMPRINT",EDGE,{"disambiguationData":[TD([[subQ4,1.0]])],"derivedFrom":subQ3}),1.0]])]});}
            var Q23;
            {var subQ1=sQuery(id+"F3.wireOp",EDGE,"E20.top");var subQ3=sQuery(id+"F3.wireOp",EDGE,"E27");var subQ4=makeQuery(id+"F3.imprint","INTERSECT",VERTEX,{"derivedFrom":[subQ1,subQ3]});Q23=makeQuery(id+"F3.imprint","IMPRINT",FACE,{"disambiguationData":[TD([[makeQuery(id+"F3.imprint","IMPRINT",EDGE,{"disambiguationData":[TD([[subQ4,1.0]])],"derivedFrom":subQ3}),1.0]])]});}
            var Q24;
            {var subQ1=sQuery(id+"F3.wireOp",EDGE,"E11.bottom");var subQ3=sQuery(id+"F3.wireOp",EDGE,"E27");var subQ4=makeQuery(id+"F3.imprint","INTERSECT",VERTEX,{"derivedFrom":[subQ1,subQ3]});Q24=makeQuery(id+"F3.imprint","IMPRINT",FACE,{"disambiguationData":[TD([[makeQuery(id+"F3.imprint","IMPRINT",EDGE,{"disambiguationData":[TD([[subQ4,1.0]])],"derivedFrom":subQ3}),1.0]])]});}
            extrude(context, id + "F4", {"entities" : qUnion([Q0, Q1, Q2, Q3, Q4, Q5, Q6, Q7, Q8, Q9, Q10, Q11, Q12, Q13, Q14, Q15, Q16, Q17, Q18, Q19, Q20, Q21, Q22, Q23, Q24]), "operationType" : NewBodyOperationType.REMOVE, "oppositeDirection" : true, "depth" : 3 * mm});
        }
        {
            var Q0;
            Q0=makeQuery(id+"F2.opExtrude","CAP_FACE",FACE,{"disambiguationData":[OSD([sQuery(id+"F0.wireOp",EDGE,"E0.bottom"),sQuery(id+"F0.wireOp",EDGE,"E0.top"),sQuery(id+"F0.wireOp",EDGE,"E0.left"),sQuery(id+"F0.wireOp",EDGE,"E0.right"),sQuery(id+"F0.wireOp",EDGE,"E3"),sQuery(id+"F0.wireOp",EDGE,"E4"),sQuery(id+"F0.wireOp",EDGE,"E5"),sQuery(id+"F0.wireOp",EDGE,"E6"),sQuery(id+"F0.wireOp",EDGE,"E7.0"),sQuery(id+"F0.wireOp",EDGE,"E8.0"),sQuery(id+"F0.wireOp",EDGE,"E9.0"),sQuery(id+"F0.wireOp",EDGE,"E10.0")])],"isStart":false});
            var sketch = newSketch(context, id + "F5", { "sketchPlane" : qUnion([Q0])});
            skLineSegment(sketch, "E28.bottom", {"start": v(-8.5, 23.5) * mm, "end": v(-7.5, 23.5) * mm});
            skLineSegment(sketch, "E28.top", {"start": v(-8.5, 22.5) * mm, "end": v(-7.5, 22.5) * mm});
            skLineSegment(sketch, "E28.left", {"start": v(-8.5, 23.5) * mm, "end": v(-8.5, 22.5) * mm});
            skLineSegment(sketch, "E28.right", {"start": v(-7.5, 23.5) * mm, "end": v(-7.5, 22.5) * mm});
            skLineSegment(sketch, "E29.bottom", {"start": v(-23.5, 8.5) * mm, "end": v(-22.5, 8.5) * mm});
            skLineSegment(sketch, "E29.top", {"start": v(-23.5, 7.5) * mm, "end": v(-22.5, 7.5) * mm});
            skLineSegment(sketch, "E29.left", {"start": v(-23.5, 8.5) * mm, "end": v(-23.5, 7.5) * mm});
            skLineSegment(sketch, "E29.right", {"start": v(-22.5, 8.5) * mm, "end": v(-22.5, 7.5) * mm});
            skLineSegment(sketch, "E30.bottom", {"start": v(7.5, 23.5) * mm, "end": v(8.5, 23.5) * mm});
            skLineSegment(sketch, "E30.top", {"start": v(7.5, 22.5) * mm, "end": v(8.5, 22.5) * mm});
            skLineSegment(sketch, "E30.left", {"start": v(7.5, 23.5) * mm, "end": v(7.5, 22.5) * mm});
            skLineSegment(sketch, "E30.right", {"start": v(8.5, 23.5) * mm, "end": v(8.5, 22.5) * mm});
            skLineSegment(sketch, "E31.bottom", {"start": v(23.5, 8.5) * mm, "end": v(22.5, 8.5) * mm});
            skLineSegment(sketch, "E31.top", {"start": v(23.5, 7.5) * mm, "end": v(22.5, 7.5) * mm});
            skLineSegment(sketch, "E31.left", {"start": v(23.5, 8.5) * mm, "end": v(23.5, 7.5) * mm});
            skLineSegment(sketch, "E31.right", {"start": v(22.5, 8.5) * mm, "end": v(22.5, 7.5) * mm});
            skLineSegment(sketch, "E32.bottom", {"start": v(23.5, -7.5) * mm, "end": v(22.5, -7.5) * mm});
            skLineSegment(sketch, "E32.top", {"start": v(23.5, -8.5) * mm, "end": v(22.5, -8.5) * mm});
            skLineSegment(sketch, "E32.left", {"start": v(23.5, -7.5) * mm, "end": v(23.5, -8.5) * mm});
            skLineSegment(sketch, "E32.right", {"start": v(22.5, -7.5) * mm, "end": v(22.5, -8.5) * mm});
            skLineSegment(sketch, "E33.bottom", {"start": v(8.5, -23.5) * mm, "end": v(7.5, -23.5) * mm});
            skLineSegment(sketch, "E33.top", {"start": v(8.5, -22.5) * mm, "end": v(7.5, -22.5) * mm});
            skLineSegment(sketch, "E33.left", {"start": v(8.5, -23.5) * mm, "end": v(8.5, -22.5) * mm});
            skLineSegment(sketch, "E33.right", {"start": v(7.5, -23.5) * mm, "end": v(7.5, -22.5) * mm});
            skLineSegment(sketch, "E34.bottom", {"start": v(-7.5, -23.5) * mm, "end": v(-8.5, -23.5) * mm});
            skLineSegment(sketch, "E34.top", {"start": v(-7.5, -22.5) * mm, "end": v(-8.5, -22.5) * mm});
            skLineSegment(sketch, "E34.left", {"start": v(-7.5, -23.5) * mm, "end": v(-7.5, -22.5) * mm});
            skLineSegment(sketch, "E34.right", {"start": v(-8.5, -23.5) * mm, "end": v(-8.5, -22.5) * mm});
            skLineSegment(sketch, "E35.bottom", {"start": v(-23.5, -8.5) * mm, "end": v(-22.5, -8.5) * mm});
            skLineSegment(sketch, "E35.top", {"start": v(-23.5, -7.5) * mm, "end": v(-22.5, -7.5) * mm});
            skLineSegment(sketch, "E35.left", {"start": v(-23.5, -8.5) * mm, "end": v(-23.5, -7.5) * mm});
            skLineSegment(sketch, "E35.right", {"start": v(-22.5, -8.5) * mm, "end": v(-22.5, -7.5) * mm});
            skSolve(sketch);
        }
        {
            var Q0;
            Q0 = qSketchRegion(id + "F5", true);
            extrude(context, id + "F6", {"entities" : qUnion([Q0]), "operationType" : NewBodyOperationType.REMOVE, "oppositeDirection" : true, "depth" : 25 * mm});
        }
        {
            var Q0;
            Q0 = qSketchRegion(id + "F5", true);
            extrude(context, id + "F7", {"entities" : qUnion([Q0]), "operationType" : NewBodyOperationType.ADD, "depth" : 2 * mm, "hasSecondDirection" : true, "secondDirectionOppositeDirection" : true, "secondDirectionDepth" : 15 * mm});
        }
    });
